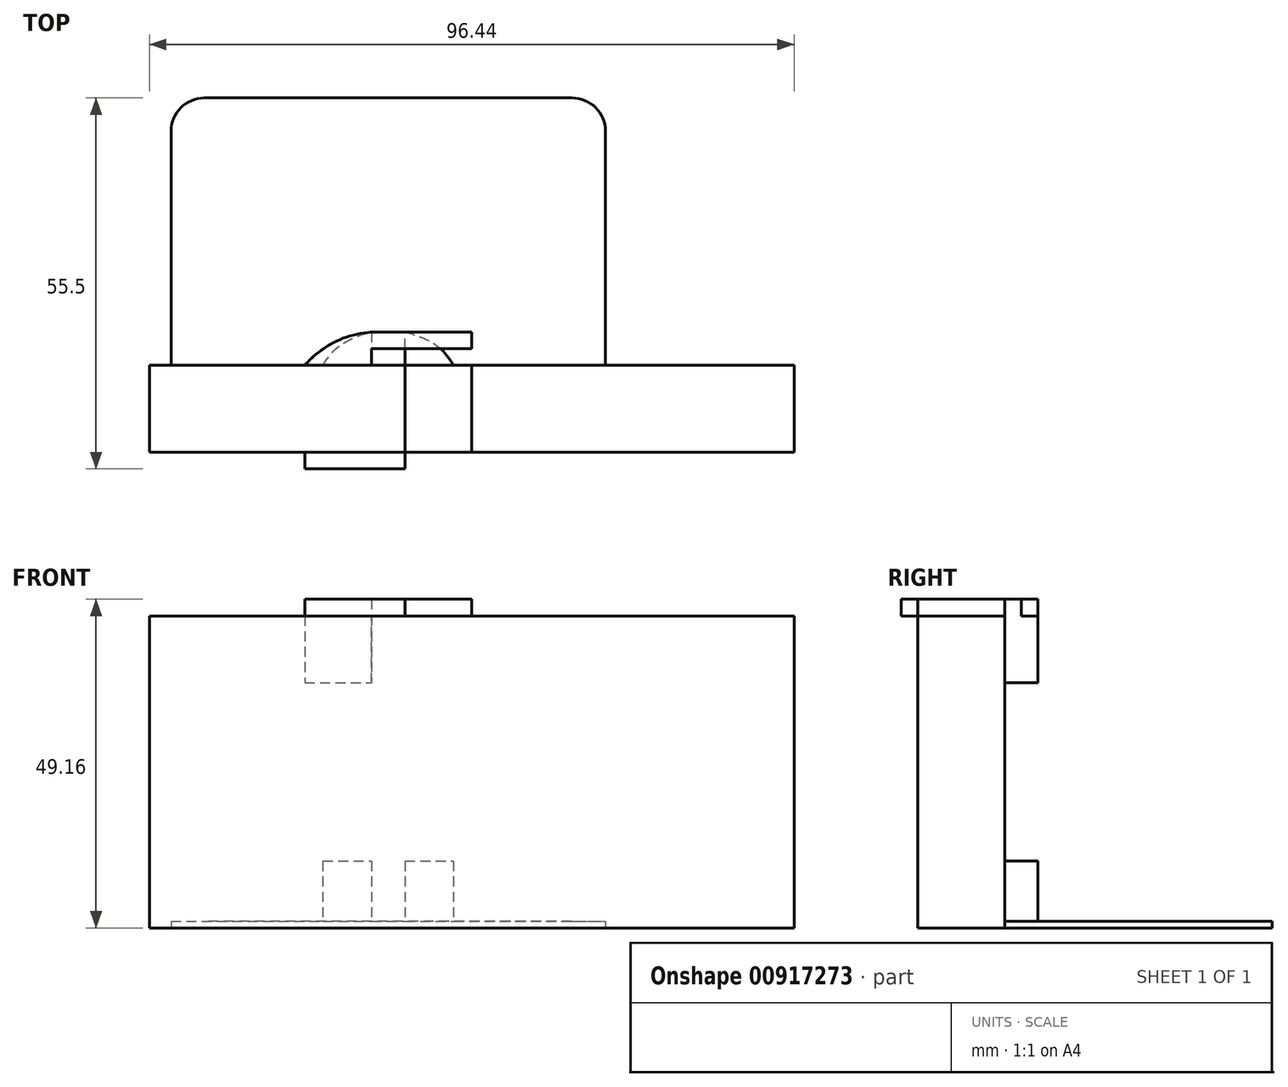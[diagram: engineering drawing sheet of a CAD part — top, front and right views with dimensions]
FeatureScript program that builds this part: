
annotation { "Feature Type Name" : "Feature", "Feature Type Description" : "" }
export const myFeature = defineFeature(function(context is Context, id is Id, definition is map)
    precondition{}
    {
        {
            var Q0;
            Q0=qCreatedBy(makeId("Front.planeOp"),FACE);
            var sketch = newSketch(context, id + "F0", { "sketchPlane" : qUnion([Q0])});
            skLineSegment(sketch, "E0.bottom", {"start": v(-48.22, 23.33) * mm, "end": v(48.22, 23.33) * mm});
            skLineSegment(sketch, "E0.top", {"start": v(-48.22, -23.33) * mm, "end": v(48.22, -23.33) * mm});
            skLineSegment(sketch, "E0.left", {"start": v(-48.22, 23.33) * mm, "end": v(-48.22, -23.33) * mm});
            skLineSegment(sketch, "E0.right", {"start": v(48.22, 23.33) * mm, "end": v(48.22, -23.33) * mm});
            skPoint(sketch, "E0.middle", {"position": v(0, 0) * mm});
            skSolve(sketch);
        }
        {
            var Q0;
            Q0 = qSketchRegion(id + "F0", true);
            extrude(context, id + "F1", {"entities" : qUnion([Q0]), "depth" : 13 * mm, "offsetDistance" : 25 * mm});
        }
        {
            var Q0;
            Q0=makeQuery(id+"F1.opExtrude","SWEPT_FACE",FACE,{"disambiguationData":[OSD([sQuery(id+"F0.wireOp",EDGE,"E0.bottom")])]});
            var sketch = newSketch(context, id + "F2", { "sketchPlane" : qUnion([Q0])});
            skLineSegment(sketch, "E1.0.0", {"start": v(48.22, 0) * mm, "end": v(-48.22, 0) * mm, "construction": true});
            skLineSegment(sketch, "E1.0.1", {"start": v(-48.22, 0) * mm, "end": v(-48.22, -13) * mm, "construction": true});
            skLineSegment(sketch, "E1.0.2", {"start": v(-48.22, -13) * mm, "end": v(48.22, -13) * mm, "construction": true});
            skLineSegment(sketch, "E1.0.3", {"start": v(48.22, -13) * mm, "end": v(48.22, 0) * mm, "construction": true});
            skLineSegment(sketch, "E2.bottom", {"start": v(0, 0) * mm, "end": v(-10, 0) * mm});
            skLineSegment(sketch, "E2.top", {"start": v(0, -13) * mm, "end": v(-10, -13) * mm});
            skLineSegment(sketch, "E2.left", {"start": v(0, 0) * mm, "end": v(0, -13) * mm});
            skLineSegment(sketch, "E2.right", {"start": v(-10, 0) * mm, "end": v(-10, -13) * mm});
            skLineSegment(sketch, "E3.bottom", {"start": v(-10, 0) * mm, "end": v(0, 0) * mm});
            skLineSegment(sketch, "E3.top", {"start": v(-10, 2.5) * mm, "end": v(0, 2.5) * mm});
            skLineSegment(sketch, "E3.left", {"start": v(-10, 0) * mm, "end": v(-10, 2.5) * mm});
            skLineSegment(sketch, "E3.right", {"start": v(0, 0) * mm, "end": v(0, 2.5) * mm});
            skLineSegment(sketch, "E4.bottom", {"start": v(-10, -13) * mm, "end": v(0, -13) * mm});
            skLineSegment(sketch, "E4.top", {"start": v(-10, -15.5) * mm, "end": v(0, -15.5) * mm});
            skLineSegment(sketch, "E4.left", {"start": v(-10, -13) * mm, "end": v(-10, -15.5) * mm});
            skLineSegment(sketch, "E4.right", {"start": v(0, -13) * mm, "end": v(0, -15.5) * mm});
            skLineSegment(sketch, "E5.bottom", {"start": v(-10, 2.5) * mm, "end": v(-15, 2.5) * mm});
            skLineSegment(sketch, "E5.top", {"start": v(-10, -15.5) * mm, "end": v(-15, -15.5) * mm});
            skLineSegment(sketch, "E5.left", {"start": v(-10, 2.5) * mm, "end": v(-10, -15.5) * mm});
            skLineSegment(sketch, "E5.right", {"start": v(-15, 2.5) * mm, "end": v(-15, -15.5) * mm});
            skLineSegment(sketch, "E6.bottom", {"start": v(-15, -15.5) * mm, "end": v(-25, -15.5) * mm});
            skLineSegment(sketch, "E6.top", {"start": v(-15, 2.5) * mm, "end": v(-25, 2.5) * mm});
            skLineSegment(sketch, "E6.left", {"start": v(-15, -15.5) * mm, "end": v(-15, 2.5) * mm});
            skLineSegment(sketch, "E6.right", {"start": v(-25, -15.5) * mm, "end": v(-25, 2.5) * mm});
            skLineSegment(sketch, "E7.bottom", {"start": v(-25, 2.5) * mm, "end": v(0, 2.5) * mm});
            skLineSegment(sketch, "E7.top", {"start": v(-25, 5) * mm, "end": v(0, 5) * mm});
            skLineSegment(sketch, "E7.left", {"start": v(-25, 2.5) * mm, "end": v(-25, 5) * mm});
            skLineSegment(sketch, "E7.right", {"start": v(0, 2.5) * mm, "end": v(0, 5) * mm});
            skLineSegment(sketch, "E8", {"start": v(-10, 2.5) * mm, "end": v(-10, 5) * mm});
            skLineSegment(sketch, "E9", {"start": v(-10, 5) * mm, "end": v(-15, 5) * mm});
            skLineSegment(sketch, "E10", {"start": v(-15, 5) * mm, "end": v(-15, 2.5) * mm});
            skSolve(sketch);
        }
        {
            var Q0;
            {var subQ0=sQuery(id+"F2.wireOp",EDGE,"E3.bottom");Q0=makeQuery(id+"F2.imprint","IMPRINT",FACE,{"disambiguationData":[TD([[makeQuery(id+"F2.imprint","IMPRINT",EDGE,{"derivedFrom":subQ0}),1.0]])]});}
            var Q1;
            Q1=makeQuery(id+"F2.imprint","IMPRINT",FACE,{"disambiguationData":[TD([[makeQuery(id+"F2.imprint","IMPRINT",EDGE,{"derivedFrom":sQuery(id+"F2.wireOp",EDGE,"E2.left")}),-1.0]])]});
            var Q2;
            {var subQ0=sQuery(id+"F2.wireOp",EDGE,"E4.bottom");Q2=makeQuery(id+"F2.imprint","IMPRINT",FACE,{"disambiguationData":[TD([[makeQuery(id+"F2.imprint","IMPRINT",EDGE,{"derivedFrom":subQ0}),-1.0]])]});}
            var Q3;
            {var subQ0=sQuery(id+"F2.wireOp",EDGE,"E6.bottom");Q3=makeQuery(id+"F2.imprint","IMPRINT",FACE,{"disambiguationData":[TD([[makeQuery(id+"F2.imprint","IMPRINT",EDGE,{"derivedFrom":subQ0}),-1.0]])]});}
            var Q4;
            {var subQ0=sQuery(id+"F2.wireOp",EDGE,"E6.left");var subQ1=sQuery(id+"F0.wireOp",EDGE,"E0.bottom");var subQ2=makeQuery(id+"F1.opExtrude","CAP_EDGE",EDGE,{"disambiguationData":[OSD([subQ1])],"isStart":false});var subQ3=makeQuery(id+"F2.imprint","INTERSECT",VERTEX,{"derivedFrom":[subQ2,subQ0]});Q4=makeQuery(id+"F2.imprint","IMPRINT",FACE,{"disambiguationData":[TD([[makeQuery(id+"F2.imprint","IMPRINT",EDGE,{"disambiguationData":[TD([[subQ3,-1.0]])],"derivedFrom":subQ0}),1.0]])]});}
            var Q5;
            {var subQ0=sQuery(id+"F2.wireOp",EDGE,"E6.top");Q5=makeQuery(id+"F2.imprint","IMPRINT",FACE,{"disambiguationData":[TD([[makeQuery(id+"F2.imprint","IMPRINT",EDGE,{"derivedFrom":subQ0}),1.0]])]});}
            var Q6;
            {var subQ1=sQuery(id+"F0.wireOp",EDGE,"E0.bottom");var subQ4=makeQuery(id+"F1.opExtrude","CAP_EDGE",EDGE,{"disambiguationData":[OSD([subQ1])],"isStart":false});var subQ6=sQuery(id+"F2.wireOp",EDGE,"E6.left");var subQ7=makeQuery(id+"F2.imprint","INTERSECT",VERTEX,{"derivedFrom":[subQ4,subQ6]});Q6=makeQuery(id+"F2.imprint","IMPRINT",FACE,{"disambiguationData":[TD([[makeQuery(id+"F2.imprint","IMPRINT",EDGE,{"disambiguationData":[TD([[subQ7,-1.0]])],"derivedFrom":subQ6}),-1.0]])]});}
            var Q7;
            {var subQ0=sQuery(id+"F2.wireOp",EDGE,"E5.top");Q7=makeQuery(id+"F2.imprint","IMPRINT",FACE,{"disambiguationData":[TD([[makeQuery(id+"F2.imprint","IMPRINT",EDGE,{"derivedFrom":subQ0}),-1.0]])]});}
            var Q8;
            {var subQ0=sQuery(id+"F2.wireOp",EDGE,"E7.bottom");var subQ1=sQuery(id+"F2.wireOp",EDGE,"E6.left");var subQ2=makeQuery(id+"F2.imprint","INTERSECT",VERTEX,{"derivedFrom":[subQ1,subQ0]});Q8=makeQuery(id+"F2.imprint","IMPRINT",FACE,{"disambiguationData":[TD([[makeQuery(id+"F2.imprint","IMPRINT",EDGE,{"disambiguationData":[TD([[subQ2,1.0]])],"derivedFrom":subQ1}),1.0]])]});}
            var Q9;
            Q9=makeQuery(id+"F2.imprint","IMPRINT",FACE,{"disambiguationData":[TD([[makeQuery(id+"F2.imprint","IMPRINT",EDGE,{"derivedFrom":sQuery(id+"F2.wireOp",EDGE,"E7.top")}),-1.0]])]});
            extrude(context, id + "F3", {"entities" : qUnion([Q0, Q1, Q2, Q3, Q4, Q5, Q6, Q7, Q8, Q9]), "depth" : 2.5 * mm, "offsetDistance" : 25 * mm});
        }
        {
            var Q0;
            Q0=makeQuery(id+"F3.opExtrude","CAP_FACE",FACE,{"disambiguationData":[OSD([sQuery(id+"F0.wireOp",EDGE,"E0.bottom"),sQuery(id+"F2.wireOp",EDGE,"E2.left"),sQuery(id+"F2.wireOp",EDGE,"E3.top"),sQuery(id+"F2.wireOp",EDGE,"E3.right"),sQuery(id+"F2.wireOp",EDGE,"E4.top"),sQuery(id+"F2.wireOp",EDGE,"E4.right"),sQuery(id+"F2.wireOp",EDGE,"E5.top"),sQuery(id+"F2.wireOp",EDGE,"E5.left"),sQuery(id+"F2.wireOp",EDGE,"E6.bottom"),sQuery(id+"F2.wireOp",EDGE,"E6.top"),sQuery(id+"F2.wireOp",EDGE,"E6.left"),sQuery(id+"F2.wireOp",EDGE,"E6.right")])],"isStart":true});
            var sketch = newSketch(context, id + "F4", { "sketchPlane" : qUnion([Q0])});
            skLineSegment(sketch, "E11.0.0", {"start": v(-48.22, 0) * mm, "end": v(48.22, 0) * mm, "construction": true});
            skLineSegment(sketch, "E11.0.1", {"start": v(48.22, 0) * mm, "end": v(48.22, 13) * mm, "construction": true});
            skLineSegment(sketch, "E11.0.2", {"start": v(48.22, 13) * mm, "end": v(-48.22, 13) * mm, "construction": true});
            skLineSegment(sketch, "E12.0.0", {"start": v(0, -5) * mm, "end": v(0, 15.5) * mm});
            skLineSegment(sketch, "E12.0.1", {"start": v(0, 15.5) * mm, "end": v(-25, 15.5) * mm});
            skLineSegment(sketch, "E12.0.2", {"start": v(-25, 15.5) * mm, "end": v(-25, -5) * mm});
            skLineSegment(sketch, "E12.0.3", {"start": v(-25, -5) * mm, "end": v(-15, -5) * mm});
            skLineSegment(sketch, "E12.0.4", {"start": v(-15, -5) * mm, "end": v(-15, 0) * mm});
            skLineSegment(sketch, "E12.0.5", {"start": v(-15, 0) * mm, "end": v(-10, 0) * mm});
            skLineSegment(sketch, "E12.0.6", {"start": v(-10, 0) * mm, "end": v(-10, -5) * mm});
            skLineSegment(sketch, "E12.0.7", {"start": v(-10, -5) * mm, "end": v(0, -5) * mm});
            skLineSegment(sketch, "E13", {"start": v(-25, 0) * mm, "end": v(0, 0) * mm});
            skLineSegment(sketch, "E14", {"start": v(-25, 13) * mm, "end": v(0, 13) * mm});
            skSolve(sketch);
        }
        {
            var Q0;
            {var subQ0=sQuery(id+"F4.wireOp",EDGE,"E12.0.1");Q0=makeQuery(id+"F4.imprint","IMPRINT",FACE,{"disambiguationData":[TD([[makeQuery(id+"F4.imprint","IMPRINT",EDGE,{"derivedFrom":subQ0}),-1.0]])]});}
            var Q1;
            {var subQ0=sQuery(id+"F4.wireOp",EDGE,"E12.0.3");Q1=makeQuery(id+"F4.imprint","IMPRINT",FACE,{"disambiguationData":[TD([[makeQuery(id+"F4.imprint","IMPRINT",EDGE,{"derivedFrom":subQ0}),1.0]])]});}
            var Q2;
            {var subQ4=sQuery(id+"F4.wireOp",EDGE,"E12.0.6");Q2=makeQuery(id+"F4.imprint","IMPRINT",FACE,{"disambiguationData":[TD([[makeQuery(id+"F4.imprint","IMPRINT",EDGE,{"derivedFrom":subQ4}),-1.0]])]});}
            extrude(context, id + "F5", {"entities" : qUnion([Q0, Q1, Q2]), "operationType" : NewBodyOperationType.ADD, "depth" : 10 * mm, "offsetDistance" : 25 * mm});
        }
        {
            var Q0;
            Q0=makeQuery(id+"F5.boolean.opBoolean","MERGE",EDGE,{"derivedFrom":[makeQuery(id+"F3.opExtrude","SWEPT_EDGE",EDGE,{"disambiguationData":[OSD([sQuery(id+"F2.wireOp",EDGE,"E7.top"),sQuery(id+"F2.wireOp",EDGE,"E7.right")])]}),makeQuery(id+"F5.opExtrude","SWEPT_EDGE",EDGE,{"disambiguationData":[OSD([sQuery(id+"F4.wireOp",EDGE,"E12.0.0"),sQuery(id+"F4.wireOp",EDGE,"E12.0.7")])]})]});
            var Q1;
            Q1=makeQuery(id+"F5.boolean.opBoolean","MERGE",EDGE,{"derivedFrom":[makeQuery(id+"F3.opExtrude","SWEPT_EDGE",EDGE,{"disambiguationData":[OSD([sQuery(id+"F2.wireOp",EDGE,"E7.top"),sQuery(id+"F2.wireOp",EDGE,"E7.left")])]}),makeQuery(id+"F5.opExtrude","SWEPT_EDGE",EDGE,{"disambiguationData":[OSD([sQuery(id+"F4.wireOp",EDGE,"E12.0.2"),sQuery(id+"F4.wireOp",EDGE,"E12.0.3")])]})]});
            fillet(context, id + "F6", {"entities" : qUnion([Q0, Q1]), "radius" : 15 * mm, "tangentPropagation" : true, "rho" : 0.5, "crossSection" : FilletCrossSection.CONIC, "allowEdgeOverflow" : false});
        }
        {
            var Q0;
            Q0=makeQuery(id+"F1.opExtrude","SWEPT_FACE",FACE,{"disambiguationData":[OSD([sQuery(id+"F0.wireOp",EDGE,"E0.top")])]});
            var sketch = newSketch(context, id + "F7", { "sketchPlane" : qUnion([Q0])});
            skLineSegment(sketch, "E15.0.0", {"start": v(-15, 0) * mm, "end": v(-22.28, 0) * mm});
            skFitSpline(sketch, "E15.0.1", {"points": [v(-22.28, 0) * mm, v(-20.61, -2.2) * mm, v(-18.19, -3.87) * mm, v(-15, -5) * mm]});
            skLineSegment(sketch, "E15.0.2", {"start": v(-15, -5) * mm, "end": v(-15, 0) * mm});
            skLineSegment(sketch, "E16.0.0", {"start": v(-10, 0) * mm, "end": v(-10, -5) * mm});
            skFitSpline(sketch, "E16.0.1", {"points": [v(-10, -5) * mm, v(-6.81, -3.87) * mm, v(-4.39, -2.2) * mm, v(-2.72, 0) * mm]});
            skLineSegment(sketch, "E16.0.2", {"start": v(-2.72, 0) * mm, "end": v(-10, 0) * mm});
            skLineSegment(sketch, "E17.bottom", {"start": v(-15, 0) * mm, "end": v(-45, 0) * mm});
            skLineSegment(sketch, "E17.top", {"start": v(-15, -40) * mm, "end": v(-45, -40) * mm});
            skLineSegment(sketch, "E17.left", {"start": v(-15, 0) * mm, "end": v(-15, -40) * mm});
            skLineSegment(sketch, "E17.right", {"start": v(-45, 0) * mm, "end": v(-45, -40) * mm});
            skLineSegment(sketch, "E18.bottom", {"start": v(-10, 0) * mm, "end": v(20, 0) * mm});
            skLineSegment(sketch, "E18.top", {"start": v(-10, -40) * mm, "end": v(20, -40) * mm});
            skLineSegment(sketch, "E18.left", {"start": v(-10, 0) * mm, "end": v(-10, -40) * mm});
            skLineSegment(sketch, "E18.right", {"start": v(20, 0) * mm, "end": v(20, -40) * mm});
            skLineSegment(sketch, "E19.bottom", {"start": v(-15, -40) * mm, "end": v(-10, -40) * mm});
            skLineSegment(sketch, "E19.top", {"start": v(-15, 0) * mm, "end": v(-10, 0) * mm});
            skLineSegment(sketch, "E19.left", {"start": v(-15, -40) * mm, "end": v(-15, 0) * mm});
            skLineSegment(sketch, "E19.right", {"start": v(-10, -40) * mm, "end": v(-10, 0) * mm});
            skSolve(sketch);
        }
        {
            var Q0;
            Q0 = qSketchRegion(id + "F7", true);
            extrude(context, id + "F8", {"entities" : qUnion([Q0]), "oppositeDirection" : true, "depth" : 1 * mm, "offsetDistance" : 25 * mm});
        }
        {
            var Q0;
            {var subQ0=sQuery(id+"F7.wireOp",EDGE,"E16.0.1");Q0=makeQuery(id+"F7.imprint","IMPRINT",FACE,{"disambiguationData":[TD([[makeQuery(id+"F7.imprint","IMPRINT",EDGE,{"derivedFrom":subQ0}),1.0]])]});}
            var Q1;
            {var subQ0=sQuery(id+"F7.wireOp",EDGE,"E15.0.1");Q1=makeQuery(id+"F7.imprint","IMPRINT",FACE,{"disambiguationData":[TD([[makeQuery(id+"F7.imprint","IMPRINT",EDGE,{"derivedFrom":subQ0}),1.0]])]});}
            extrude(context, id + "F9", {"entities" : qUnion([Q0, Q1]), "operationType" : NewBodyOperationType.ADD, "oppositeDirection" : true, "depth" : 10 * mm, "offsetDistance" : 25 * mm});
        }
        {
            var Q0;
            Q0=makeQuery(id+"F8.opExtrude","SWEPT_EDGE",EDGE,{"disambiguationData":[OSD([sQuery(id+"F7.wireOp",EDGE,"E18.top"),sQuery(id+"F7.wireOp",EDGE,"E18.right")])]});
            var Q1;
            Q1=makeQuery(id+"F8.opExtrude","SWEPT_EDGE",EDGE,{"disambiguationData":[OSD([sQuery(id+"F7.wireOp",EDGE,"E17.top"),sQuery(id+"F7.wireOp",EDGE,"E17.right")])]});
            fillet(context, id + "F10", {"entities" : qUnion([Q0, Q1]), "radius" : 5 * mm, "tangentPropagation" : true, "allowEdgeOverflow" : false});
        }
    });
